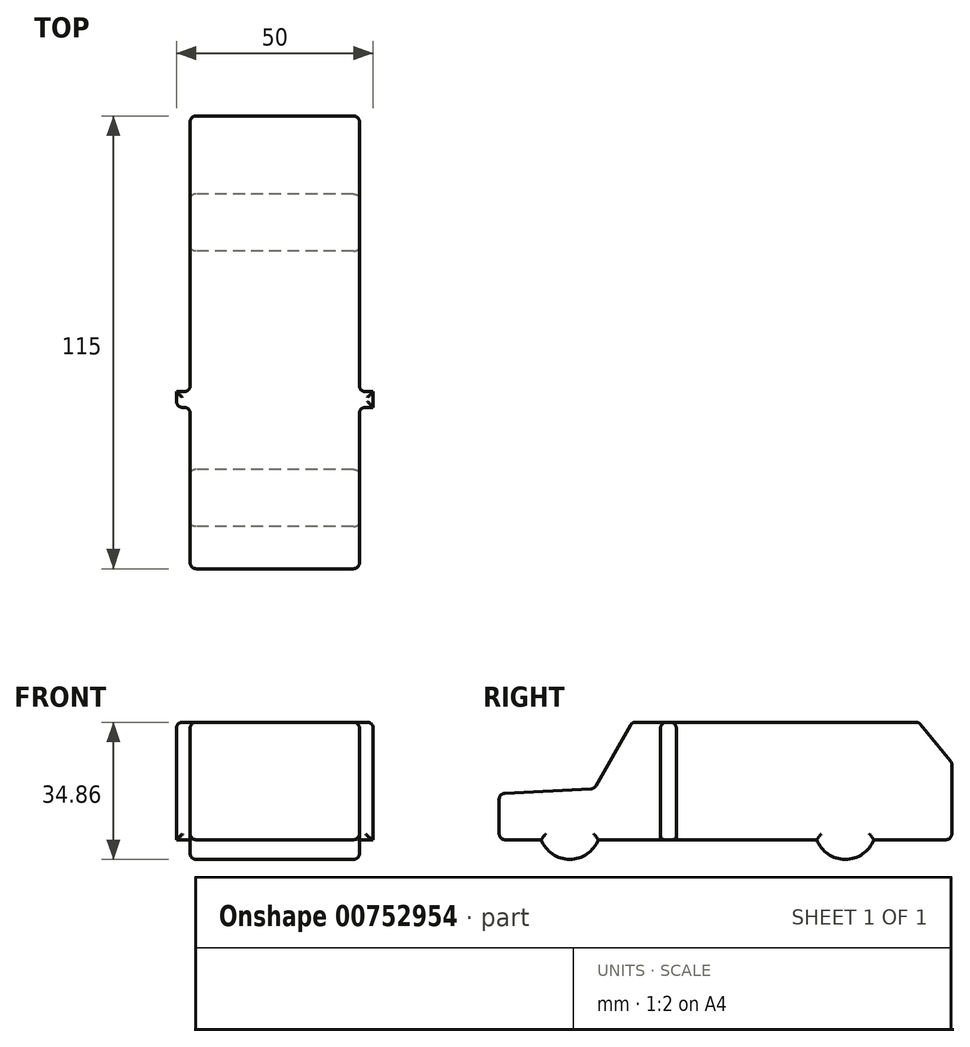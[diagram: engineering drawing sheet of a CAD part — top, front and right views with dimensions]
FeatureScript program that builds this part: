
annotation { "Feature Type Name" : "Feature", "Feature Type Description" : "" }
export const myFeature = defineFeature(function(context is Context, id is Id, definition is map)
    precondition{}
    {
        {
            var Q0;
            Q0=qCreatedBy(makeId("Top.planeOp"),FACE);
            var sketch = newSketch(context, id + "F0", { "sketchPlane" : qUnion([Q0])});
            skLineSegment(sketch, "E0.bottom", {"start": v(21.5, 57.5) * mm, "end": v(-21.5, 57.5) * mm});
            skLineSegment(sketch, "E0.top", {"start": v(21.5, -57.5) * mm, "end": v(-21.5, -57.5) * mm});
            skLineSegment(sketch, "E0.left", {"start": v(21.5, 57.5) * mm, "end": v(21.5, -57.5) * mm});
            skLineSegment(sketch, "E0.right", {"start": v(-21.5, 57.5) * mm, "end": v(-21.5, -57.5) * mm});
            skPoint(sketch, "E0.middle", {"position": v(0, 0) * mm});
            skLineSegment(sketch, "E1.bottom", {"start": v(25, -12.5) * mm, "end": v(-25, -12.5) * mm});
            skLineSegment(sketch, "E1.top", {"start": v(25, -16.5) * mm, "end": v(-25, -16.5) * mm});
            skLineSegment(sketch, "E1.left", {"start": v(25, -12.5) * mm, "end": v(25, -16.5) * mm});
            skLineSegment(sketch, "E1.right", {"start": v(-25, -12.5) * mm, "end": v(-25, -16.5) * mm});
            skPoint(sketch, "E1.middle", {"position": v(0, -14.5) * mm});
            skSolve(sketch);
        }
        {
            var Q0;
            {var subQ0=sQuery(id+"F0.wireOp",EDGE,"E0.bottom");Q0=makeQuery(id+"F0.imprint","IMPRINT",FACE,{"disambiguationData":[TD([[makeQuery(id+"F0.imprint","IMPRINT",EDGE,{"derivedFrom":subQ0}),1.0]])]});}
            var Q1;
            {var subQ0=sQuery(id+"F0.wireOp",EDGE,"E0.top");Q1=makeQuery(id+"F0.imprint","IMPRINT",FACE,{"disambiguationData":[TD([[makeQuery(id+"F0.imprint","IMPRINT",EDGE,{"derivedFrom":subQ0}),-1.0]])]});}
            var Q2;
            {var subQ0=sQuery(id+"F0.wireOp",EDGE,"E1.bottom");var subQ1=sQuery(id+"F0.wireOp",EDGE,"E0.left");var subQ2=makeQuery(id+"F0.imprint","INTERSECT",VERTEX,{"derivedFrom":[subQ1,subQ0]});Q2=makeQuery(id+"F0.imprint","IMPRINT",FACE,{"disambiguationData":[TD([[makeQuery(id+"F0.imprint","IMPRINT",EDGE,{"disambiguationData":[TD([[subQ2,-1.0]])],"derivedFrom":subQ1}),-1.0]])]});}
            var Q3;
            {var subQ5=sQuery(id+"F0.wireOp",EDGE,"E1.right");Q3=makeQuery(id+"F0.imprint","IMPRINT",FACE,{"disambiguationData":[TD([[makeQuery(id+"F0.imprint","IMPRINT",EDGE,{"derivedFrom":subQ5}),1.0]])]});}
            var Q4;
            {var subQ5=sQuery(id+"F0.wireOp",EDGE,"E1.left");Q4=makeQuery(id+"F0.imprint","IMPRINT",FACE,{"disambiguationData":[TD([[makeQuery(id+"F0.imprint","IMPRINT",EDGE,{"derivedFrom":subQ5}),-1.0]])]});}
            extrude(context, id + "F1", {"entities" : qUnion([Q0, Q1, Q2, Q3, Q4]), "depth" : 35 * mm, "offsetDistance" : 25 * mm});
        }
        {
            var Q0;
            Q0=makeQuery(id+"F1.opExtrude","SWEPT_FACE",FACE,{"disambiguationData":[OSD([sQuery(id+"F0.wireOp",EDGE,"E1.right")])]});
            var sketch = newSketch(context, id + "F2", { "sketchPlane" : qUnion([Q0])});
            skLineSegment(sketch, "E2", {"start": v(-57.65, 0.14) * mm, "end": v(-57.65, 24.58) * mm});
            skLineSegment(sketch, "E3", {"start": v(-57.65, 24.58) * mm, "end": v(-48.97, 35.14) * mm});
            skLineSegment(sketch, "E4", {"start": v(-48.97, 35.14) * mm, "end": v(23.6, 35.14) * mm});
            skLineSegment(sketch, "E5", {"start": v(23.6, 35.14) * mm, "end": v(33.37, 18.12) * mm});
            skLineSegment(sketch, "E6", {"start": v(33.37, 18.12) * mm, "end": v(57.57, 16.84) * mm});
            skLineSegment(sketch, "E7", {"start": v(57.57, 16.84) * mm, "end": v(57.57, 5.14) * mm});
            skLineSegment(sketch, "E8", {"start": v(57.57, 5.14) * mm, "end": v(-57.65, 5.14) * mm});
            skLineSegment(sketch, "E9", {"start": v(-57.65, 5.14) * mm, "end": v(-57.65, 24.58) * mm});
            skCircle(sketch, "E10", {"center": v(-30.43, 7.9) * mm, "radius": 7.75 * mm});
            skCircle(sketch, "E11", {"center": v(39.57, 7.9) * mm, "radius": 7.75 * mm});
            skLineSegment(sketch, "E12.bottom", {"start": v(-63.87, 40.73) * mm, "end": v(69.37, 40.73) * mm});
            skLineSegment(sketch, "E12.top", {"start": v(-63.87, -8.9) * mm, "end": v(69.37, -8.9) * mm});
            skLineSegment(sketch, "E12.left", {"start": v(-63.87, 40.73) * mm, "end": v(-63.87, -8.9) * mm});
            skLineSegment(sketch, "E12.right", {"start": v(69.37, 40.73) * mm, "end": v(69.37, -8.9) * mm});
            skSolve(sketch);
        }
        {
            var Q0;
            Q0=makeQuery(id+"F2.imprint","IMPRINT",FACE,{"disambiguationData":[TD([[makeQuery(id+"F2.imprint","IMPRINT",EDGE,{"derivedFrom":sQuery(id+"F2.wireOp",EDGE,"E3")}),1.0]])]});
            var Q1;
            {var subQ1=sQuery(id+"F0.wireOp",EDGE,"E1.right");var subQ6=makeQuery(id+"F1.opExtrude","CAP_EDGE",EDGE,{"disambiguationData":[OSD([subQ1])],"isStart":true});Q1=makeQuery(id+"F2.imprint","IMPRINT",FACE,{"disambiguationData":[TD([[makeQuery(id+"F2.imprint","IMPRINT",EDGE,{"derivedFrom":subQ6}),1.0]])]});}
            extrude(context, id + "F3", {"entities" : qUnion([Q0, Q1]), "operationType" : NewBodyOperationType.REMOVE, "oppositeDirection" : true, "depth" : 71.3 * mm, "offsetDistance" : 25 * mm});
        }
        {
            var Q0;
            {var subQ0=sQuery(id+"F0.wireOp",EDGE,"E0.right");Q0=makeQuery(id+"F1.opExtrude","CAP_EDGE",EDGE,{"disambiguationData":[OSD([subQ0]),TDD([makeQuery(id+"F0.imprint","IMPRINT",EDGE,{"disambiguationData":[TD([[makeQuery(id+"F0.imprint","INTERSECT",VERTEX,{"derivedFrom":[sQuery(id+"F0.wireOp",EDGE,"E0.bottom"),subQ0]}),-1.0]])],"derivedFrom":subQ0})])],"isStart":false});}
            var Q1;
            {var subQ0=sQuery(id+"F0.wireOp",EDGE,"E0.right");Q1=makeQuery(id+"F3.boolean.opBoolean","INTERSECT",EDGE,{"derivedFrom":[makeQuery(id+"F1.opExtrude","SWEPT_FACE",FACE,{"disambiguationData":[OSD([subQ0]),TDD([makeQuery(id+"F0.imprint","IMPRINT",EDGE,{"disambiguationData":[TD([[makeQuery(id+"F0.imprint","INTERSECT",VERTEX,{"derivedFrom":[sQuery(id+"F0.wireOp",EDGE,"E0.top"),subQ0]}),1.0]])],"derivedFrom":subQ0})])]}),makeQuery(id+"F3.opExtrude","SWEPT_FACE",FACE,{"disambiguationData":[OSD([sQuery(id+"F2.wireOp",EDGE,"E5")])]})]});}
            var Q2;
            Q2=makeQuery(id+"F3.boolean.opBoolean","INTERSECT",EDGE,{"derivedFrom":[makeQuery(id+"F1.opExtrude","CAP_FACE",FACE,{"disambiguationData":[OSD([sQuery(id+"F0.wireOp",EDGE,"E0.bottom"),sQuery(id+"F0.wireOp",EDGE,"E0.top"),sQuery(id+"F0.wireOp",EDGE,"E0.left"),sQuery(id+"F0.wireOp",EDGE,"E0.right"),sQuery(id+"F0.wireOp",EDGE,"E1.bottom"),sQuery(id+"F0.wireOp",EDGE,"E1.top"),sQuery(id+"F0.wireOp",EDGE,"E1.left"),sQuery(id+"F0.wireOp",EDGE,"E1.right")])],"isStart":false}),makeQuery(id+"F3.opExtrude","SWEPT_FACE",FACE,{"disambiguationData":[OSD([sQuery(id+"F2.wireOp",EDGE,"E5")])]})]});
            var Q3;
            Q3=makeQuery(id+"F3.boolean.opBoolean","COPY",EDGE,{"derivedFrom":makeQuery(id+"F3.opExtrude","SWEPT_EDGE",EDGE,{"disambiguationData":[OSD([sQuery(id+"F2.wireOp",EDGE,"E5"),sQuery(id+"F2.wireOp",EDGE,"E6")])]})});
            var Q4;
            {var subQ0=sQuery(id+"F0.wireOp",EDGE,"E0.right");Q4=makeQuery(id+"F1.opExtrude","CAP_EDGE",EDGE,{"disambiguationData":[OSD([subQ0]),TDD([makeQuery(id+"F0.imprint","IMPRINT",EDGE,{"disambiguationData":[TD([[makeQuery(id+"F0.imprint","INTERSECT",VERTEX,{"derivedFrom":[sQuery(id+"F0.wireOp",EDGE,"E0.top"),subQ0]}),1.0]])],"derivedFrom":subQ0})])],"isStart":false});}
            var Q5;
            Q5=makeQuery(id+"F3.boolean.opBoolean","INTERSECT",EDGE,{"derivedFrom":[makeQuery(id+"F1.opExtrude","SWEPT_FACE",FACE,{"disambiguationData":[OSD([sQuery(id+"F0.wireOp",EDGE,"E0.top")])]}),makeQuery(id+"F3.opExtrude","SWEPT_FACE",FACE,{"disambiguationData":[OSD([sQuery(id+"F2.wireOp",EDGE,"E6")])]})]});
            var Q6;
            {var subQ0=sQuery(id+"F0.wireOp",EDGE,"E0.left");Q6=makeQuery(id+"F1.opExtrude","SWEPT_FACE",FACE,{"disambiguationData":[OSD([subQ0]),TDD([makeQuery(id+"F0.imprint","IMPRINT",EDGE,{"disambiguationData":[TD([[makeQuery(id+"F0.imprint","INTERSECT",VERTEX,{"derivedFrom":[sQuery(id+"F0.wireOp",EDGE,"E0.top"),subQ0]}),1.0]])],"derivedFrom":subQ0})])]});}
            var Q7;
            {var subQ0=sQuery(id+"F0.wireOp",EDGE,"E0.left");Q7=makeQuery(id+"F3.boolean.opBoolean","INTERSECT",EDGE,{"derivedFrom":[makeQuery(id+"F1.opExtrude","SWEPT_FACE",FACE,{"disambiguationData":[OSD([subQ0]),TDD([makeQuery(id+"F0.imprint","IMPRINT",EDGE,{"disambiguationData":[TD([[makeQuery(id+"F0.imprint","INTERSECT",VERTEX,{"derivedFrom":[sQuery(id+"F0.wireOp",EDGE,"E0.top"),subQ0]}),1.0]])],"derivedFrom":subQ0})])]}),makeQuery(id+"F3.opExtrude","SWEPT_FACE",FACE,{"disambiguationData":[OSD([sQuery(id+"F2.wireOp",EDGE,"E5")])]})]});}
            var Q8;
            {var subQ0=sQuery(id+"F2.wireOp",EDGE,"E8");Q8=makeQuery(id+"F3.boolean.opBoolean","INTERSECT",EDGE,{"derivedFrom":[makeQuery(id+"F1.opExtrude","SWEPT_FACE",FACE,{"disambiguationData":[OSD([sQuery(id+"F0.wireOp",EDGE,"E0.top")])]}),makeQuery(id+"F3.opExtrude","SWEPT_FACE",FACE,{"disambiguationData":[OSD([subQ0]),TDD([makeQuery(id+"F2.imprint","IMPRINT",EDGE,{"disambiguationData":[TD([[makeQuery(id+"F2.imprint","INTERSECT",VERTEX,{"derivedFrom":[sQuery(id+"F2.wireOp",EDGE,"E7"),subQ0]}),-1.0]])],"derivedFrom":subQ0})])]})]});}
            var Q9;
            Q9=makeQuery(id+"F1.opExtrude","SWEPT_EDGE",EDGE,{"disambiguationData":[OSD([sQuery(id+"F0.wireOp",EDGE,"E0.right"),sQuery(id+"F0.wireOp",EDGE,"E1.top")])]});
            var Q10;
            {var subQ0=sQuery(id+"F0.wireOp",EDGE,"E1.top");Q10=makeQuery(id+"F1.opExtrude","CAP_EDGE",EDGE,{"disambiguationData":[OSD([subQ0]),TDD([makeQuery(id+"F0.imprint","IMPRINT",EDGE,{"disambiguationData":[TD([[makeQuery(id+"F0.imprint","INTERSECT",VERTEX,{"derivedFrom":[subQ0,sQuery(id+"F0.wireOp",EDGE,"E1.right")]}),1.0]])],"derivedFrom":subQ0})])],"isStart":false});}
            var Q11;
            Q11=makeQuery(id+"F1.opExtrude","SWEPT_EDGE",EDGE,{"disambiguationData":[OSD([sQuery(id+"F0.wireOp",EDGE,"E1.top"),sQuery(id+"F0.wireOp",EDGE,"E1.right")])]});
            var Q12;
            {var subQ0=sQuery(id+"F2.wireOp",EDGE,"E8");var subQ1=sQuery(id+"F0.wireOp",EDGE,"E1.right");var subQ3=sQuery(id+"F0.wireOp",EDGE,"E1.top");var subQ4=makeQuery(id+"F2.imprint","INTERSECT",VERTEX,{"derivedFrom":[makeQuery(id+"F1.opExtrude","SWEPT_EDGE",EDGE,{"disambiguationData":[OSD([subQ3,subQ1])]}),subQ0]});Q12=makeQuery(id+"F3.boolean.opBoolean","INTERSECT",EDGE,{"derivedFrom":[makeQuery(id+"F1.opExtrude","SWEPT_FACE",FACE,{"disambiguationData":[OSD([subQ3]),TDD([makeQuery(id+"F0.imprint","IMPRINT",EDGE,{"disambiguationData":[TD([[makeQuery(id+"F0.imprint","INTERSECT",VERTEX,{"derivedFrom":[subQ3,subQ1]}),1.0]])],"derivedFrom":subQ3})])]}),makeQuery(id+"F3.opExtrude","SWEPT_FACE",FACE,{"disambiguationData":[OSD([subQ0]),TDD([makeQuery(id+"F2.imprint","IMPRINT",EDGE,{"disambiguationData":[TD([[makeQuery(id+"F2.imprint","INTERSECT",VERTEX,{"disambiguationData":[OD(1.0)],"derivedFrom":[subQ0,sQuery(id+"F2.wireOp",EDGE,"E11")]}),-1.0]])],"derivedFrom":subQ0}),makeQuery(id+"F2.imprint","IMPRINT",EDGE,{"disambiguationData":[TD([[subQ4,-1.0]])],"derivedFrom":subQ0}),makeQuery(id+"F2.imprint","IMPRINT",EDGE,{"disambiguationData":[TD([[makeQuery(id+"F2.imprint","INTERSECT",VERTEX,{"disambiguationData":[OD(0.0)],"derivedFrom":[subQ0,sQuery(id+"F2.wireOp",EDGE,"E10")]}),1.0]])],"derivedFrom":subQ0})])]})]});}
            var Q13;
            {var subQ0=sQuery(id+"F2.wireOp",EDGE,"E8");var subQ1=sQuery(id+"F0.wireOp",EDGE,"E1.right");var subQ3=makeQuery(id+"F2.imprint","INTERSECT",VERTEX,{"derivedFrom":[makeQuery(id+"F1.opExtrude","SWEPT_EDGE",EDGE,{"disambiguationData":[OSD([sQuery(id+"F0.wireOp",EDGE,"E1.top"),subQ1])]}),subQ0]});Q13=makeQuery(id+"F3.boolean.opBoolean","COPY",EDGE,{"derivedFrom":makeQuery(id+"F3.opExtrude","CAP_EDGE",EDGE,{"disambiguationData":[OSD([subQ0]),TDD([makeQuery(id+"F2.imprint","IMPRINT",EDGE,{"disambiguationData":[TD([[makeQuery(id+"F2.imprint","INTERSECT",VERTEX,{"disambiguationData":[OD(1.0)],"derivedFrom":[subQ0,sQuery(id+"F2.wireOp",EDGE,"E11")]}),-1.0]])],"derivedFrom":subQ0}),makeQuery(id+"F2.imprint","IMPRINT",EDGE,{"disambiguationData":[TD([[subQ3,-1.0]])],"derivedFrom":subQ0}),makeQuery(id+"F2.imprint","IMPRINT",EDGE,{"disambiguationData":[TD([[makeQuery(id+"F2.imprint","INTERSECT",VERTEX,{"disambiguationData":[OD(0.0)],"derivedFrom":[subQ0,sQuery(id+"F2.wireOp",EDGE,"E10")]}),1.0]])],"derivedFrom":subQ0})])],"isStart":true})});}
            var Q14;
            {var subQ0=sQuery(id+"F0.wireOp",EDGE,"E0.right");Q14=makeQuery(id+"F1.opExtrude","SWEPT_FACE",FACE,{"disambiguationData":[OSD([subQ0]),TDD([makeQuery(id+"F0.imprint","IMPRINT",EDGE,{"disambiguationData":[TD([[makeQuery(id+"F0.imprint","INTERSECT",VERTEX,{"derivedFrom":[sQuery(id+"F0.wireOp",EDGE,"E0.bottom"),subQ0]}),-1.0]])],"derivedFrom":subQ0})])]});}
            var Q15;
            Q15=makeQuery(id+"F1.opExtrude","CAP_FACE",FACE,{"disambiguationData":[OSD([sQuery(id+"F0.wireOp",EDGE,"E0.bottom"),sQuery(id+"F0.wireOp",EDGE,"E0.top"),sQuery(id+"F0.wireOp",EDGE,"E0.left"),sQuery(id+"F0.wireOp",EDGE,"E0.right"),sQuery(id+"F0.wireOp",EDGE,"E1.bottom"),sQuery(id+"F0.wireOp",EDGE,"E1.top"),sQuery(id+"F0.wireOp",EDGE,"E1.left"),sQuery(id+"F0.wireOp",EDGE,"E1.right")])],"isStart":false});
            var Q16;
            {var subQ0=sQuery(id+"F0.wireOp",EDGE,"E0.left");Q16=makeQuery(id+"F1.opExtrude","SWEPT_FACE",FACE,{"disambiguationData":[OSD([subQ0]),TDD([makeQuery(id+"F0.imprint","IMPRINT",EDGE,{"disambiguationData":[TD([[makeQuery(id+"F0.imprint","INTERSECT",VERTEX,{"derivedFrom":[sQuery(id+"F0.wireOp",EDGE,"E0.bottom"),subQ0]}),-1.0]])],"derivedFrom":subQ0})])]});}
            var Q17;
            Q17=makeQuery(id+"F3.boolean.opBoolean","COPY",FACE,{"derivedFrom":makeQuery(id+"F3.opExtrude","SWEPT_FACE",FACE,{"disambiguationData":[OSD([sQuery(id+"F2.wireOp",EDGE,"E3")])]})});
            var Q18;
            Q18=makeQuery(id+"F1.opExtrude","SWEPT_FACE",FACE,{"disambiguationData":[OSD([sQuery(id+"F0.wireOp",EDGE,"E0.bottom")])]});
            var Q19;
            {var subQ0=sQuery(id+"F0.wireOp",EDGE,"E0.right");Q19=makeQuery(id+"F1.opExtrude","SWEPT_FACE",FACE,{"disambiguationData":[OSD([subQ0]),TDD([makeQuery(id+"F0.imprint","IMPRINT",EDGE,{"disambiguationData":[TD([[makeQuery(id+"F0.imprint","INTERSECT",VERTEX,{"derivedFrom":[sQuery(id+"F0.wireOp",EDGE,"E0.top"),subQ0]}),1.0]])],"derivedFrom":subQ0})])]});}
            fillet(context, id + "F4", {"entities" : qUnion([Q0, Q1, Q2, Q3, Q4, Q5, Q6, Q7, Q8, Q9, Q10, Q11, Q12, Q13, Q14, Q15, Q16, Q17, Q18, Q19]), "radius" : 1.5 * mm, "tangentPropagation" : true, "allowEdgeOverflow" : false});
        }
    });
